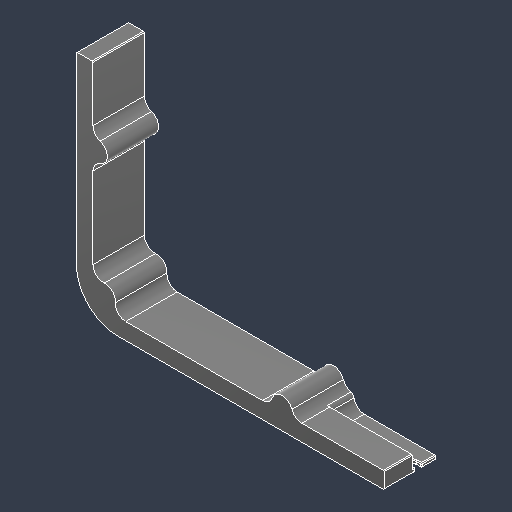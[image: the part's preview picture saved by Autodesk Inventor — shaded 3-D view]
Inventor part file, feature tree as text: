
AUTODESK INVENTOR PART (.ipt)
format: ipt  version: 2023.4 (Build 274418000, 418)  size: 165,888 bytes
history: native  units: mm
features: sketch x5, other x3
ambient origin geometry x8: Origin, YZ Plane, XZ Plane, XY Plane, X Axis, Y Axis, Z Axis, Center Point
bodies: Solid1 (feature_tree)
feature tree (8):
  other  "Corner Top Right.ipt"
  other  "Solid1::Corner Top Right.ipt"
  other  "TaggingFeature1"
  sketch  "Sketch1"  dims[d0=10.0mm]
  sketch  "Sketch2"
  sketch  "Sketch3"
  sketch  "Sketch4"
  sketch  "Sketch5"
